# Revit family: Faucet-Single-DXV-Modulus-D35120102RB_Series
name_source: partatom
category: Plumbing Fixtures
units: mm (PartAtom-declared; Revit-internal decimal feet)

## family parameters
Always vertical = No
Cut with Voids When Loaded = Yes
OmniClass Number = 23.45.55.14
OmniClass Title = Single Faucets
Part Type = Normal
Room Calculation Point = No
Round Connector Dimension = Use Radius
Shared = Yes
Work Plane-Based = Yes

## types (3) — shared parameters
ADA Compliant = Yes
Assembly Code = D2020300
CWFU = 1.5
CalGreen Compliant = Yes
Default Elevation = 0"
Description = DXV Modulus Single Lever Lavatory Faucet
Flow Rate = 1.2 gpm (4.5 L/min)
HWFU = 1.5
Height = 5"
Installation Type = Deck Mounted
Length = 6 15/16"
Manufacturer = DXV
Price = Prices may vary. Please consult Manufacturer Rep for most up-to-date price list.
Product Documentation Link = https://dxv01.blob.core.windows.net
Product Page URL = https://www.dxv.com
Revised Date = 06/07/2022
Tempered Water Connection = Yes
Tempered Water Connection Diameter = 3/8"
Tempered Water Connection Radius = 3/16"
URL = https://www.dxv.com
Vent Connection = No
WFU = 2
Waste Connection = No
Width = 2 9/16"

## per-type parameters (varying)
| type | CW Connection | Finish | HW Connection | Material |
| D35120102RB.100 | Yes | Brass-DXV-100-Polished Chrome | Yes | Brass-DXV-100-Polished Chrome |
| D35120102RB.144 | Yes | Brass-DXV-144-Brushed Nickel | Yes | Brass-DXV-144-Brushed Nickel |
| D35120102RB.150 | No | Brass-DXV-150-Platinum Nickel | No | Brass-DXV-150-Platinum Nickel |

note: column(s) folded — value = type name in every type: Model

## geometry (parser evidence)
native form markers: Sweep x2
no freeform markers — native parametric forms only
